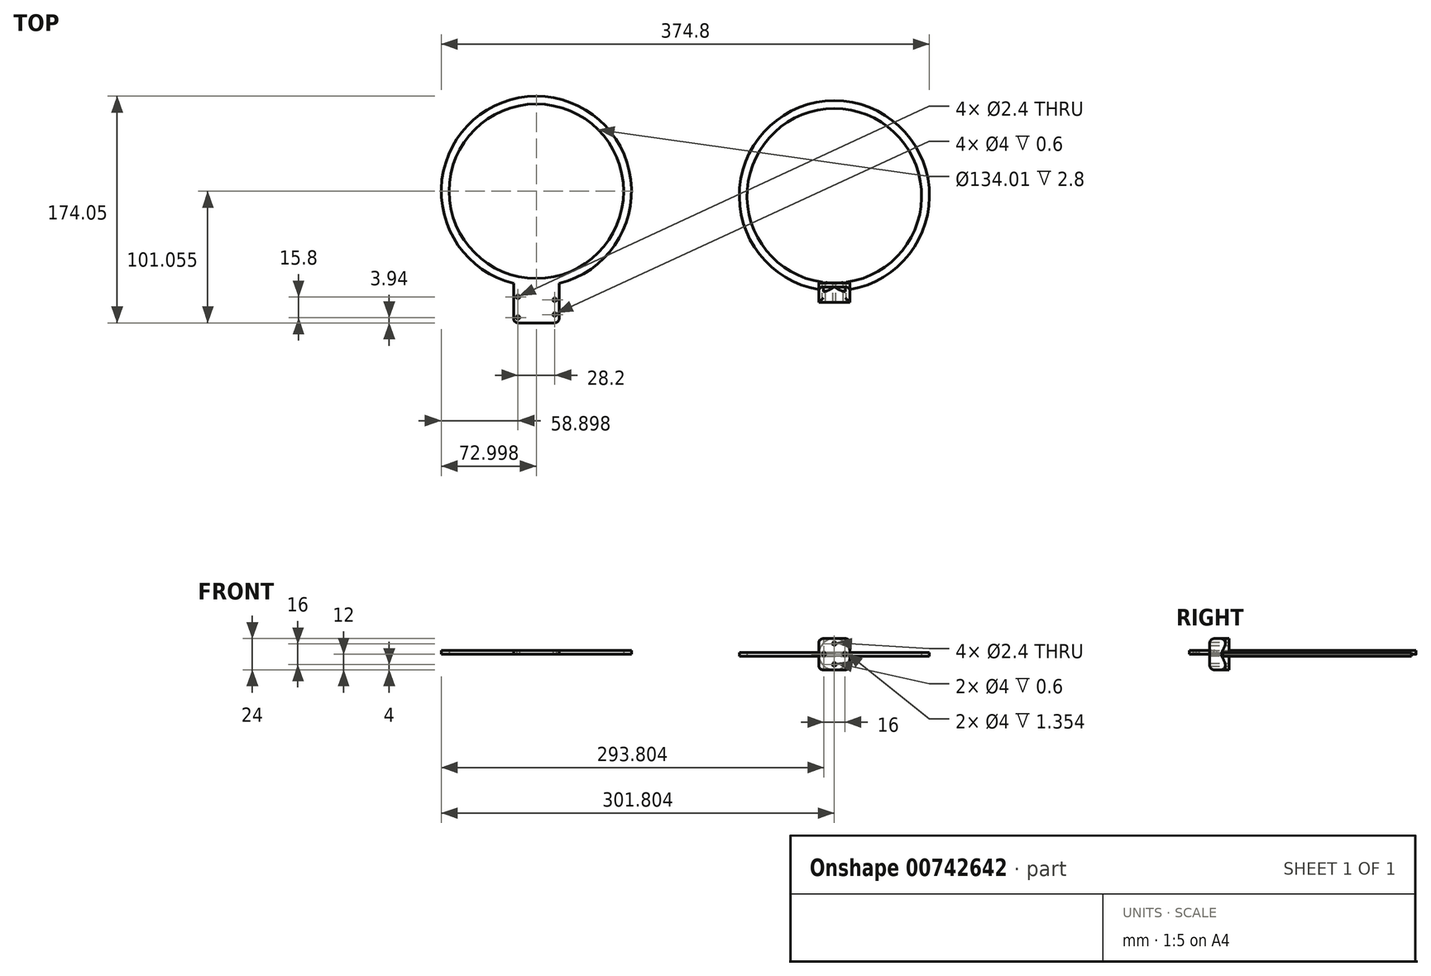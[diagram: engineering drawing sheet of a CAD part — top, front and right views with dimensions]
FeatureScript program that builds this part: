
annotation { "Feature Type Name" : "Feature", "Feature Type Description" : "" }
export const myFeature = defineFeature(function(context is Context, id is Id, definition is map)
    precondition{}
    {
        {
            var Q0;
            Q0=qCreatedBy(makeId("Top.planeOp"),FACE);
            var sketch = newSketch(context, id + "F0", { "sketchPlane" : qUnion([Q0])});
            skPoint(sketch, "E0", {"position": v(-58.92, 13.55) * mm});
            skPoint(sketch, "E1", {"position": v(-58.92, -2.25) * mm});
            skPoint(sketch, "E2", {"position": v(-30.72, 11.3) * mm});
            skPoint(sketch, "E3", {"position": v(-30.72, 0) * mm});
            skLineSegment(sketch, "E4", {"start": v(-58.92, 13.55) * mm, "end": v(-58.92, -2.25) * mm, "construction": true});
            skLineSegment(sketch, "E5", {"start": v(-30.72, 11.3) * mm, "end": v(-30.72, 0) * mm, "construction": true});
            skLineSegment(sketch, "E6", {"start": v(-58.92, 5.65) * mm, "end": v(-30.72, 5.65) * mm, "construction": true});
            skLineSegment(sketch, "E7.bottom", {"start": v(-58.82, 17.5) * mm, "end": v(-30.82, 17.5) * mm});
            skLineSegment(sketch, "E7.top", {"start": v(-58.82, -6.2) * mm, "end": v(-30.82, -6.2) * mm});
            skLineSegment(sketch, "E7.left", {"start": v(-62.32, 14) * mm, "end": v(-62.32, -2.7) * mm});
            skLineSegment(sketch, "E7.right", {"start": v(-27.32, 14) * mm, "end": v(-27.32, -2.7) * mm});
            skPoint(sketch, "E7.middle", {"position": v(-44.82, 5.65) * mm});
            skPoint(sketch, "E8.visualSharp", {"position": v(-27.32, 17.5) * mm});
            skArc(sketch, "E8.filletArc", {"start": v(-27.32, 14) * mm, "mid": v(-28.35, 16.47) * mm, "end": v(-30.82, 17.5) * mm});
            skPoint(sketch, "E9.visualSharp", {"position": v(-27.32, -6.2) * mm});
            skArc(sketch, "E9.filletArc", {"start": v(-30.82, -6.2) * mm, "mid": v(-28.35, -5.17) * mm, "end": v(-27.32, -2.7) * mm});
            skPoint(sketch, "E10.visualSharp", {"position": v(-62.32, 17.5) * mm});
            skArc(sketch, "E10.filletArc", {"start": v(-58.82, 17.5) * mm, "mid": v(-61.3, 16.47) * mm, "end": v(-62.32, 14) * mm});
            skPoint(sketch, "E11.visualSharp", {"position": v(-62.32, -6.2) * mm});
            skArc(sketch, "E11.filletArc", {"start": v(-62.32, -2.7) * mm, "mid": v(-61.3, -5.17) * mm, "end": v(-58.82, -6.2) * mm});
            skLineSegment(sketch, "E12.bottom", {"start": v(-62.32, 14) * mm, "end": v(-27.32, 14) * mm});
            skLineSegment(sketch, "E12.top", {"start": v(-58.82, 27.5) * mm, "end": v(-30.82, 27.5) * mm});
            skLineSegment(sketch, "E12.left", {"start": v(-62.32, 14) * mm, "end": v(-62.32, 24) * mm});
            skLineSegment(sketch, "E12.right", {"start": v(-27.32, 14) * mm, "end": v(-27.32, 24) * mm});
            skPoint(sketch, "E13.visualSharp", {"position": v(-62.32, 27.5) * mm});
            skArc(sketch, "E13.filletArc", {"start": v(-58.82, 27.5) * mm, "mid": v(-61.3, 26.47) * mm, "end": v(-62.32, 24) * mm});
            skPoint(sketch, "E14.visualSharp", {"position": v(-27.32, 27.5) * mm});
            skArc(sketch, "E14.filletArc", {"start": v(-27.32, 24) * mm, "mid": v(-28.35, 26.47) * mm, "end": v(-30.82, 27.5) * mm});
            skCircle(sketch, "E15", {"center": v(-44.82, 94.86) * mm, "radius": 73 * mm});
            skPoint(sketch, "E15.third.point", {"position": v(-35.15, 167.22) * mm});
            skCircle(sketch, "E16", {"center": v(-44.82, 94.86) * mm, "radius": 67 * mm});
            skLineSegment(sketch, "E17", {"start": v(22.14, 92.57) * mm, "end": v(28.14, 92.57) * mm, "construction": true});
            skCircle(sketch, "E18", {"center": v(183.98, 91.4) * mm, "radius": 73 * mm});
            skPoint(sketch, "E18.third.point", {"position": v(193.66, 163.76) * mm});
            skCircle(sketch, "E19", {"center": v(183.98, 91.4) * mm, "radius": 67 * mm});
            skLineSegment(sketch, "E20", {"start": v(250.95, 89.1) * mm, "end": v(256.95, 89.1) * mm, "construction": true});
            skLineSegment(sketch, "E21.bottom", {"start": v(171.98, 19.4) * mm, "end": v(195.98, 19.4) * mm});
            skLineSegment(sketch, "E21.top", {"start": v(171.98, 9.4) * mm, "end": v(195.98, 9.4) * mm});
            skLineSegment(sketch, "E21.left", {"start": v(171.98, 19.4) * mm, "end": v(171.98, 9.4) * mm});
            skLineSegment(sketch, "E21.right", {"start": v(195.98, 19.4) * mm, "end": v(195.98, 9.4) * mm});
            skLineSegment(sketch, "E22.top", {"start": v(175.48, 21.4) * mm, "end": v(192.48, 21.4) * mm});
            skLineSegment(sketch, "E22.left", {"start": v(171.98, 17.9) * mm, "end": v(171.98, 19.4) * mm});
            skLineSegment(sketch, "E22.right", {"start": v(195.98, 17.9) * mm, "end": v(195.98, 19.4) * mm});
            skPoint(sketch, "E23.visualSharp", {"position": v(171.98, 21.4) * mm});
            skArc(sketch, "E23.filletArc", {"start": v(175.48, 21.4) * mm, "mid": v(173, 20.37) * mm, "end": v(171.98, 17.9) * mm});
            skPoint(sketch, "E24.visualSharp", {"position": v(195.98, 21.4) * mm});
            skArc(sketch, "E24.filletArc", {"start": v(195.98, 17.9) * mm, "mid": v(194.96, 20.37) * mm, "end": v(192.48, 21.4) * mm});
            skSolve(sketch);
        }
        {
            var Q0;
            {var subQ4=sQuery(id+"F0.wireOp",EDGE,"E10.filletArc");Q0=makeQuery(id+"F0.imprint","IMPRINT",FACE,{"disambiguationData":[TD([[makeQuery(id+"F0.imprint","IMPRINT",EDGE,{"derivedFrom":subQ4}),-1.0]])]});}
            var Q1;
            {var subQ4=sQuery(id+"F0.wireOp",EDGE,"E8.filletArc");Q1=makeQuery(id+"F0.imprint","IMPRINT",FACE,{"disambiguationData":[TD([[makeQuery(id+"F0.imprint","IMPRINT",EDGE,{"derivedFrom":subQ4}),-1.0]])]});}
            var Q2;
            Q2=makeQuery(id+"F0.imprint","IMPRINT",FACE,{"disambiguationData":[TD([[makeQuery(id+"F0.imprint","IMPRINT",EDGE,{"derivedFrom":sQuery(id+"F0.wireOp",EDGE,"E7.top")}),1.0]])]});
            var Q3;
            {var subQ1=sQuery(id+"F0.wireOp",EDGE,"E8.filletArc");Q3=makeQuery(id+"F0.imprint","IMPRINT",FACE,{"disambiguationData":[TD([[makeQuery(id+"F0.imprint","IMPRINT",EDGE,{"derivedFrom":subQ1}),1.0]])]});}
            var Q4;
            Q4=makeQuery(id+"F0.imprint","IMPRINT",FACE,{"disambiguationData":[TD([[makeQuery(id+"F0.imprint","IMPRINT",EDGE,{"derivedFrom":sQuery(id+"F0.wireOp",EDGE,"E12.top")}),1.0]])]});
            var Q5;
            Q5=makeQuery(id+"F0.imprint","IMPRINT",FACE,{"disambiguationData":[TD([[makeQuery(id+"F0.imprint","IMPRINT",EDGE,{"derivedFrom":sQuery(id+"F0.wireOp",EDGE,"E12.top")}),-1.0]])]});
            extrude(context, id + "F1", {"entities" : qUnion([Q0, Q1, Q2, Q3, Q4, Q5]), "depth" : 2.8 * mm, "offsetDistance" : 25 * mm});
        }
        {
            var Q0;
            Q0=sQuery(id+"F0.wireOp",VERTEX,"E2");
            var Q1;
            Q1=sQuery(id+"F0.wireOp",VERTEX,"E0");
            var Q2;
            Q2=sQuery(id+"F0.wireOp",VERTEX,"E1");
            var Q3;
            Q3=sQuery(id+"F0.wireOp",VERTEX,"E3");
            var Q4;
            Q4=makeQuery(id+"F1.opExtrude","SWEPT_BODY",BODY,{"disambiguationData":[OSD([sQuery(id+"F0.wireOp",EDGE,"E7.top"),sQuery(id+"F0.wireOp",EDGE,"E7.left"),sQuery(id+"F0.wireOp",EDGE,"E7.right"),sQuery(id+"F0.wireOp",EDGE,"E9.filletArc"),sQuery(id+"F0.wireOp",EDGE,"E11.filletArc"),sQuery(id+"F0.wireOp",EDGE,"21f06866-b8bc-43f6-b5f0-5e511e5c2d49"),sQuery(id+"F0.wireOp",EDGE,"kw2o2a1a-Mqzd-fq17-weTZ-fKeXg6PqmsJ2")])]});
            hole(context, id + "F2", {"style" : HoleStyle.C_BORE, "endStyle" : HoleEndStyle.THROUGH, "oppositeDirection" : true, "holeDiameter" : 2.4 * mm, "cBoreDiameter" : 4 * mm, "cBoreDepth" : 0.6 * mm, "majorDiameter" : 5 * mm, "isTappedThrough" : true, "tappedDepth" : 10.5 * mm, "tapClearance" : 3, "locations" : qUnion([Q0, Q1, Q2, Q3]), "scope" : qUnion([Q4])});
        }
        {
            var Q0;
            {var subQ0=sQuery(id+"F0.wireOp",EDGE,"310ac831-cfd7-4464-8d7f-cd2eb16299b2.left");Q0=makeQuery(id+"F0.imprint","IMPRINT",FACE,{"disambiguationData":[TD([[makeQuery(id+"F0.imprint","IMPRINT",EDGE,{"derivedFrom":subQ0}),-1.0]])]});}
            var Q1;
            {var subQ3=sQuery(id+"F0.wireOp",EDGE,"lwNftqxF-o1Ol-nbgC-4CEq-xsXfHTjq9fld");Q1=makeQuery(id+"F0.imprint","IMPRINT",FACE,{"disambiguationData":[TD([[makeQuery(id+"F0.imprint","IMPRINT",EDGE,{"derivedFrom":subQ3}),-1.0]])]});}
            var Q2;
            Q2=makeQuery(id+"F0.imprint","IMPRINT",FACE,{"disambiguationData":[TD([[makeQuery(id+"F0.imprint","IMPRINT",EDGE,{"derivedFrom":sQuery(id+"F0.wireOp",EDGE,"E21.top")}),1.0]])]});
            var Q3;
            {var subQ0=sQuery(id+"F0.wireOp",EDGE,"E23.filletArc");var subQ1=sQuery(id+"F0.wireOp",EDGE,"E18");var subQ2=makeQuery(id+"F0.imprint","INTERSECT",VERTEX,{"derivedFrom":[subQ1,subQ0]});Q3=makeQuery(id+"F0.imprint","IMPRINT",FACE,{"disambiguationData":[TD([[makeQuery(id+"F0.imprint","IMPRINT",EDGE,{"disambiguationData":[TD([[subQ2,-1.0]])],"derivedFrom":subQ1}),1.0]])]});}
            var Q4;
            {var subQ5=sQuery(id+"F0.wireOp",EDGE,"E22.top");Q4=makeQuery(id+"F0.imprint","IMPRINT",FACE,{"disambiguationData":[TD([[makeQuery(id+"F0.imprint","IMPRINT",EDGE,{"derivedFrom":subQ5}),-1.0]])]});}
            extrude(context, id + "F3", {"entities" : qUnion([Q0, Q1, Q2, Q3, Q4]), "operationType" : NewBodyOperationType.ADD, "depth" : 12 * mm, "offsetDistance" : 25 * mm, "hasSecondDirection" : true, "secondDirectionOppositeDirection" : true, "secondDirectionDepth" : 12 * mm});
        }
        {
            var Q0;
            Q0=makeQuery(id+"F0.imprint","IMPRINT",FACE,{"disambiguationData":[TD([[makeQuery(id+"F0.imprint","IMPRINT",EDGE,{"derivedFrom":sQuery(id+"F0.wireOp",EDGE,"E19")}),-1.0]])]});
            extrude(context, id + "F4", {"entities" : qUnion([Q0]), "operationType" : NewBodyOperationType.ADD, "depth" : 1.4 * mm, "offsetDistance" : 25 * mm, "hasSecondDirection" : true, "secondDirectionOppositeDirection" : true, "secondDirectionDepth" : 1.4 * mm});
        }
        {
            var Q0;
            Q0=makeQuery(id+"F3.opExtrude","SWEPT_FACE",FACE,{"disambiguationData":[OSD([sQuery(id+"F0.wireOp",EDGE,"E21.top")])]});
            var sketch = newSketch(context, id + "F5", { "sketchPlane" : qUnion([Q0])});
            skPoint(sketch, "E25", {"position": v(183.98, 0) * mm});
            skPoint(sketch, "E25.positionSnap0", {"position": v(195.98, 0) * mm});
            skPoint(sketch, "E25.positionSnap1", {"position": v(183.98, 12) * mm});
            skCircle(sketch, "E26", {"center": v(183.98, 0) * mm, "radius": 8 * mm});
            skPoint(sketch, "E27", {"position": v(183.98, 8) * mm});
            skPoint(sketch, "E28", {"position": v(183.98, -8) * mm});
            skPoint(sketch, "E29", {"position": v(191.98, 0) * mm});
            skPoint(sketch, "E30", {"position": v(175.98, 0) * mm});
            skCircle(sketch, "E31", {"center": v(183.98, 0) * mm, "radius": 12 * mm});
            skSolve(sketch);
        }
        {
            var Q0;
            Q0 = qSketchRegion(id + "F5", true);
            var Q1;
            Q1=makeQuery(id+"F5.imprint","IMPRINT",FACE,{"disambiguationData":[TD([[makeQuery(id+"F5.imprint","IMPRINT",EDGE,{"derivedFrom":sQuery(id+"F5.wireOp",EDGE,"E26")}),1.0]])]});
            extrude(context, id + "F6", {"entities" : qUnion([Q0, Q1]), "operationType" : NewBodyOperationType.ADD, "oppositeDirection" : true, "depth" : 15 * mm, "offsetDistance" : 25 * mm});
        }
        {
            var Q0;
            Q0=makeQuery(id+"F6.opExtrude","CAP_FACE",FACE,{"disambiguationData":[OSD([sQuery(id+"F5.wireOp",EDGE,"E31")])],"isStart":false});
            var sketch = newSketch(context, id + "F7", { "sketchPlane" : qUnion([Q0])});
            skPoint(sketch, "E32", {"position": v(-183.98, -8) * mm});
            skPoint(sketch, "E33", {"position": v(-183.98, 8) * mm});
            skPoint(sketch, "E34", {"position": v(-175.98, 0) * mm});
            skPoint(sketch, "E35", {"position": v(-191.98, 0) * mm});
            skSolve(sketch);
        }
        {
            var Q0;
            Q0=sQuery(id+"F7.wireOp",VERTEX,"E35");
            var Q1;
            Q1=sQuery(id+"F7.wireOp",VERTEX,"E32");
            var Q2;
            Q2=sQuery(id+"F7.wireOp",VERTEX,"E33");
            var Q3;
            Q3=sQuery(id+"F7.wireOp",VERTEX,"E34");
            var Q4;
            Q4=makeQuery(id+"F3.opExtrude","SWEPT_BODY",BODY,{"disambiguationData":[OSD([sQuery(id+"F0.wireOp",EDGE,"E21.top"),sQuery(id+"F0.wireOp",EDGE,"E21.left"),sQuery(id+"F0.wireOp",EDGE,"E21.right"),sQuery(id+"F0.wireOp",EDGE,"E22.top"),sQuery(id+"F0.wireOp",EDGE,"E23.filletArc"),sQuery(id+"F0.wireOp",EDGE,"E24.filletArc")])]});
            hole(context, id + "F8", {"style" : HoleStyle.C_BORE, "endStyle" : HoleEndStyle.THROUGH, "holeDiameter" : 2.4 * mm, "cBoreDiameter" : 4 * mm, "cBoreDepth" : 0.6 * mm, "majorDiameter" : 5 * mm, "isTappedThrough" : true, "tappedDepth" : 10.5 * mm, "tapClearance" : 3, "locations" : qUnion([Q0, Q1, Q2, Q3]), "scope" : qUnion([Q4])});
        }
        {
            var Q0;
            Q0=sQuery(id+"F7.wireOp",VERTEX,"E35");
            var Q1;
            Q1=sQuery(id+"F7.wireOp",VERTEX,"E34");
            var Q2;
            Q2=makeQuery(id+"F3.opExtrude","SWEPT_BODY",BODY,{"disambiguationData":[OSD([sQuery(id+"F0.wireOp",EDGE,"E21.top"),sQuery(id+"F0.wireOp",EDGE,"E21.left"),sQuery(id+"F0.wireOp",EDGE,"E21.right"),sQuery(id+"F0.wireOp",EDGE,"E22.top"),sQuery(id+"F0.wireOp",EDGE,"E23.filletArc"),sQuery(id+"F0.wireOp",EDGE,"E24.filletArc")])]});
            hole(context, id + "F9", {"style" : HoleStyle.SIMPLE, "endStyle" : HoleEndStyle.BLIND, "oppositeDirection" : true, "holeDiameter" : 4 * mm, "majorDiameter" : 5 * mm, "holeDepth" : 8 * mm, "isTappedThrough" : true, "tappedDepth" : 10.5 * mm, "tapClearance" : 3, "locations" : qUnion([Q0, Q1]), "scope" : qUnion([Q2])});
        }
        {
            var Q0;
            Q0=makeQuery(id+"F3.opExtrude","CAP_FACE",FACE,{"disambiguationData":[OSD([sQuery(id+"F0.wireOp",EDGE,"E21.top"),sQuery(id+"F0.wireOp",EDGE,"E21.left"),sQuery(id+"F0.wireOp",EDGE,"E21.right"),sQuery(id+"F0.wireOp",EDGE,"E22.top"),sQuery(id+"F0.wireOp",EDGE,"E23.filletArc"),sQuery(id+"F0.wireOp",EDGE,"E24.filletArc")])],"isStart":false});
            var Q1;
            Q1=makeQuery(id+"F3.opExtrude","CAP_FACE",FACE,{"disambiguationData":[OSD([sQuery(id+"F0.wireOp",EDGE,"E21.top"),sQuery(id+"F0.wireOp",EDGE,"E21.left"),sQuery(id+"F0.wireOp",EDGE,"E21.right"),sQuery(id+"F0.wireOp",EDGE,"E22.top"),sQuery(id+"F0.wireOp",EDGE,"E23.filletArc"),sQuery(id+"F0.wireOp",EDGE,"E24.filletArc")])],"isStart":true});
            fillet(context, id + "F10", {"entities" : qUnion([Q0, Q1]), "radius" : 3.5 * mm, "tangentPropagation" : true, "allowEdgeOverflow" : false});
        }
    });
